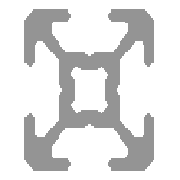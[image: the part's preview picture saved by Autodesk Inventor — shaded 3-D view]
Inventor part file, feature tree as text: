
AUTODESK INVENTOR PART (.ipt)
format: ipt  version: 2015 (Build 190159000, 159)  size: 386,048 bytes
history: native  units: mm
features: other x3, extrude x1, sketch x1
ambient origin geometry x8: Origin, YZ Plane, XZ Plane, XY Plane, X Axis, Y Axis, Z Axis, Center Point
bodies: Body1 (feature_tree)
feature tree (5):
  other  "Blocks"
  extrude  "Extrusion3"  [1 undecoded]
  sketch  "Sketch1"  dims[d23=0.0mm]
  other  "20x20"
  other  "20x20:1"
note: 1 required parameter value undecoded (feature->parameter linkage not recoverable at this tier; creation-order binding heuristic only, values carry confidence <= 0.55)
